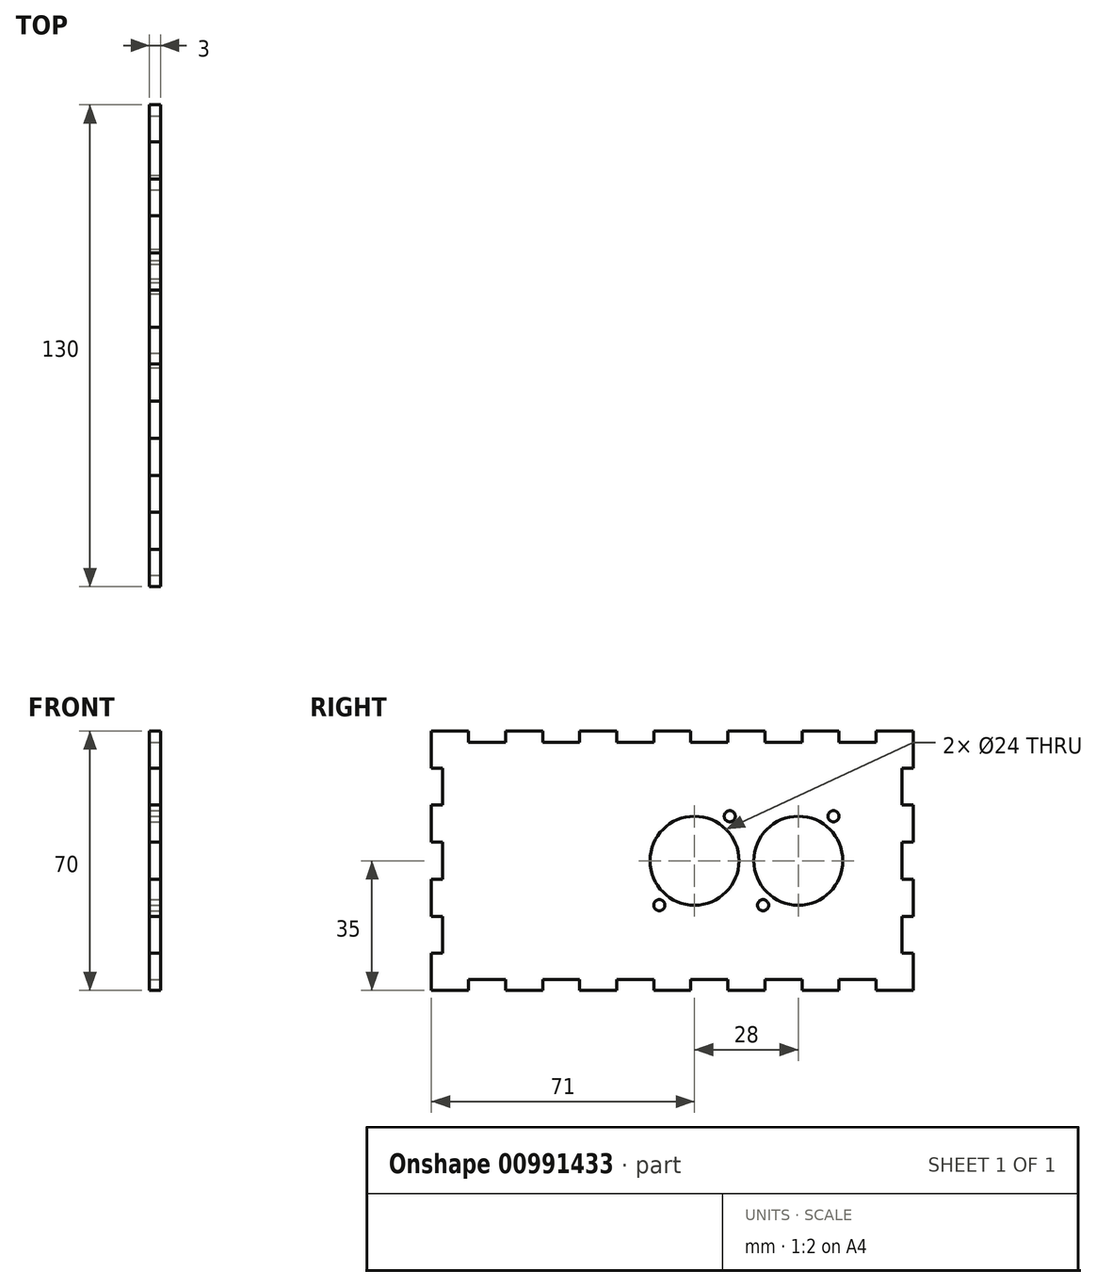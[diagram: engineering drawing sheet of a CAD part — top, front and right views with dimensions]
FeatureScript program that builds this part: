
annotation { "Feature Type Name" : "Feature", "Feature Type Description" : "" }
export const myFeature = defineFeature(function(context is Context, id is Id, definition is map)
    precondition{}
    {
        {
            var Q0;
            Q0=qCreatedBy(makeId("Right.planeOp"),FACE);
            var sketch = newSketch(context, id + "F0", { "sketchPlane" : qUnion([Q0])});
            skLineSegment(sketch, "E0.bottom", {"start": v(65, -35) * mm, "end": v(-65, -35) * mm});
            skLineSegment(sketch, "E0.top", {"start": v(65, 35) * mm, "end": v(-65, 35) * mm});
            skLineSegment(sketch, "E0.left", {"start": v(65, -35) * mm, "end": v(65, 35) * mm});
            skLineSegment(sketch, "E0.right", {"start": v(-65, -35) * mm, "end": v(-65, 35) * mm});
            skPoint(sketch, "E0.middle", {"position": v(0, 0) * mm});
            skSolve(sketch);
        }
        {
            var Q0;
            Q0 = qSketchRegion(id + "F0", true);
            extrude(context, id + "F1", {"entities" : qUnion([Q0]), "depth" : 3 * mm, "offsetDistance" : 25 * mm});
        }
        {
            var Q0;
            Q0=makeQuery(id+"F1.opExtrude","CAP_FACE",FACE,{"disambiguationData":[OSD([sQuery(id+"F0.wireOp",EDGE,"E0.bottom"),sQuery(id+"F0.wireOp",EDGE,"E0.top"),sQuery(id+"F0.wireOp",EDGE,"E0.left"),sQuery(id+"F0.wireOp",EDGE,"E0.right")])],"isStart":false});
            var sketch = newSketch(context, id + "F2", { "sketchPlane" : qUnion([Q0])});
            skLineSegment(sketch, "E1.bottom", {"start": v(-65, 25) * mm, "end": v(-62, 25) * mm});
            skLineSegment(sketch, "E1.top", {"start": v(-65, 15) * mm, "end": v(-62, 15) * mm});
            skLineSegment(sketch, "E1.left", {"start": v(-65, 25) * mm, "end": v(-65, 15) * mm});
            skLineSegment(sketch, "E1.right", {"start": v(-62, 25) * mm, "end": v(-62, 15) * mm});
            skLineSegment(sketch, "E2.0.1.0", {"start": v(-65, 5) * mm, "end": v(-65, -5) * mm});
            skLineSegment(sketch, "E2.0.1.1", {"start": v(-65, 5) * mm, "end": v(-62, 5) * mm});
            skLineSegment(sketch, "E2.0.1.2", {"start": v(-62, 5) * mm, "end": v(-62, -5) * mm});
            skLineSegment(sketch, "E2.0.1.3", {"start": v(-65, -5) * mm, "end": v(-62, -5) * mm});
            skLineSegment(sketch, "E2.0.2.0", {"start": v(-65, -15) * mm, "end": v(-65, -25) * mm});
            skLineSegment(sketch, "E2.0.2.1", {"start": v(-65, -15) * mm, "end": v(-62, -15) * mm});
            skLineSegment(sketch, "E2.0.2.2", {"start": v(-62, -15) * mm, "end": v(-62, -25) * mm});
            skLineSegment(sketch, "E2.0.2.3", {"start": v(-65, -25) * mm, "end": v(-62, -25) * mm});
            skLineSegment(sketch, "E2.direction1", {"start": v(-65, 15) * mm, "end": v(-35, 15) * mm, "construction": true});
            skLineSegment(sketch, "E2.direction2", {"start": v(-65, 15) * mm, "end": v(-65, -5) * mm, "construction": true});
            skLineSegment(sketch, "E3", {"start": v(0, 35) * mm, "end": v(0, -35) * mm, "construction": true});
            skLineSegment(sketch, "E4.MirrorCS", {"start": v(65, 5) * mm, "end": v(65, -5) * mm});
            skLineSegment(sketch, "E5.MirrorCS", {"start": v(62, 5) * mm, "end": v(62, -5) * mm});
            skLineSegment(sketch, "E6.MirrorCS", {"start": v(65, -5) * mm, "end": v(62, -5) * mm});
            skLineSegment(sketch, "E7.MirrorCS", {"start": v(65, 15) * mm, "end": v(65, -5) * mm, "construction": true});
            skLineSegment(sketch, "E8.MirrorCS", {"start": v(65, 25) * mm, "end": v(62, 25) * mm});
            skLineSegment(sketch, "E9.MirrorCS", {"start": v(65, -15) * mm, "end": v(65, -25) * mm});
            skLineSegment(sketch, "E10.MirrorCS", {"start": v(65, 15) * mm, "end": v(62, 15) * mm});
            skLineSegment(sketch, "E11.MirrorCS", {"start": v(62, -15) * mm, "end": v(62, -25) * mm});
            skLineSegment(sketch, "E12.MirrorCS", {"start": v(62, 25) * mm, "end": v(62, 15) * mm});
            skLineSegment(sketch, "E13.MirrorCS", {"start": v(65, -25) * mm, "end": v(62, -25) * mm});
            skLineSegment(sketch, "E14.MirrorCS", {"start": v(65, -15) * mm, "end": v(62, -15) * mm});
            skLineSegment(sketch, "E15.MirrorCS", {"start": v(65, 25) * mm, "end": v(65, 15) * mm});
            skLineSegment(sketch, "E16.MirrorCS", {"start": v(65, 5) * mm, "end": v(62, 5) * mm});
            skLineSegment(sketch, "E17", {"start": v(-65, 0) * mm, "end": v(65, 0) * mm, "construction": true});
            skLineSegment(sketch, "E18.bottom", {"start": v(-55, -35) * mm, "end": v(-45, -35) * mm});
            skLineSegment(sketch, "E18.top", {"start": v(-55, -32) * mm, "end": v(-45, -32) * mm});
            skLineSegment(sketch, "E18.left", {"start": v(-55, -35) * mm, "end": v(-55, -32) * mm});
            skLineSegment(sketch, "E18.right", {"start": v(-45, -35) * mm, "end": v(-45, -32) * mm});
            skLineSegment(sketch, "E19.1.0.0", {"start": v(-35, -35) * mm, "end": v(-35, -32) * mm});
            skLineSegment(sketch, "E19.1.0.1", {"start": v(-35, -32) * mm, "end": v(-25, -32) * mm});
            skLineSegment(sketch, "E19.1.0.2", {"start": v(-25, -35) * mm, "end": v(-25, -32) * mm});
            skLineSegment(sketch, "E19.1.0.3", {"start": v(-35, -35) * mm, "end": v(-25, -35) * mm});
            skLineSegment(sketch, "E19.2.0.0", {"start": v(-15, -35) * mm, "end": v(-15, -32) * mm});
            skLineSegment(sketch, "E19.2.0.1", {"start": v(-15, -32) * mm, "end": v(-5, -32) * mm});
            skLineSegment(sketch, "E19.2.0.2", {"start": v(-5, -35) * mm, "end": v(-5, -32) * mm});
            skLineSegment(sketch, "E19.2.0.3", {"start": v(-15, -35) * mm, "end": v(-5, -35) * mm});
            skLineSegment(sketch, "E19.3.0.0", {"start": v(5, -35) * mm, "end": v(5, -32) * mm});
            skLineSegment(sketch, "E19.3.0.1", {"start": v(5, -32) * mm, "end": v(15, -32) * mm});
            skLineSegment(sketch, "E19.3.0.2", {"start": v(15, -35) * mm, "end": v(15, -32) * mm});
            skLineSegment(sketch, "E19.3.0.3", {"start": v(5, -35) * mm, "end": v(15, -35) * mm});
            skLineSegment(sketch, "E19.4.0.0", {"start": v(25, -35) * mm, "end": v(25, -32) * mm});
            skLineSegment(sketch, "E19.4.0.1", {"start": v(25, -32) * mm, "end": v(35, -32) * mm});
            skLineSegment(sketch, "E19.4.0.2", {"start": v(35, -35) * mm, "end": v(35, -32) * mm});
            skLineSegment(sketch, "E19.4.0.3", {"start": v(25, -35) * mm, "end": v(35, -35) * mm});
            skLineSegment(sketch, "E19.5.0.0", {"start": v(45, -35) * mm, "end": v(45, -32) * mm});
            skLineSegment(sketch, "E19.5.0.1", {"start": v(45, -32) * mm, "end": v(55, -32) * mm});
            skLineSegment(sketch, "E19.5.0.2", {"start": v(55, -35) * mm, "end": v(55, -32) * mm});
            skLineSegment(sketch, "E19.5.0.3", {"start": v(45, -35) * mm, "end": v(55, -35) * mm});
            skLineSegment(sketch, "E19.direction1", {"start": v(-55, -35) * mm, "end": v(-35, -35) * mm, "construction": true});
            skLineSegment(sketch, "E20.MirrorCS", {"start": v(-55, 35) * mm, "end": v(-45, 35) * mm});
            skLineSegment(sketch, "E21.MirrorCS", {"start": v(-25, 35) * mm, "end": v(-25, 32) * mm});
            skLineSegment(sketch, "E22.MirrorCS", {"start": v(45, 32) * mm, "end": v(55, 32) * mm});
            skLineSegment(sketch, "E23.MirrorCS", {"start": v(45, 35) * mm, "end": v(55, 35) * mm});
            skLineSegment(sketch, "E24.MirrorCS", {"start": v(-35, 35) * mm, "end": v(-25, 35) * mm});
            skLineSegment(sketch, "E25.MirrorCS", {"start": v(-35, 32) * mm, "end": v(-25, 32) * mm});
            skLineSegment(sketch, "E26.MirrorCS", {"start": v(-5, 35) * mm, "end": v(-5, 32) * mm});
            skLineSegment(sketch, "E27.MirrorCS", {"start": v(-55, 35) * mm, "end": v(-55, 32) * mm});
            skLineSegment(sketch, "E28.MirrorCS", {"start": v(5, 32) * mm, "end": v(15, 32) * mm});
            skLineSegment(sketch, "E29.MirrorCS", {"start": v(55, 35) * mm, "end": v(55, 32) * mm});
            skLineSegment(sketch, "E30.MirrorCS", {"start": v(5, 35) * mm, "end": v(15, 35) * mm});
            skLineSegment(sketch, "E31.MirrorCS", {"start": v(-15, 32) * mm, "end": v(-5, 32) * mm});
            skLineSegment(sketch, "E32.MirrorCS", {"start": v(5, 35) * mm, "end": v(5, 32) * mm});
            skLineSegment(sketch, "E33.MirrorCS", {"start": v(-55, 32) * mm, "end": v(-45, 32) * mm});
            skLineSegment(sketch, "E34.MirrorCS", {"start": v(-55, 35) * mm, "end": v(-35, 35) * mm, "construction": true});
            skLineSegment(sketch, "E35.MirrorCS", {"start": v(35, 35) * mm, "end": v(35, 32) * mm});
            skLineSegment(sketch, "E36.MirrorCS", {"start": v(25, 35) * mm, "end": v(25, 32) * mm});
            skLineSegment(sketch, "E37.MirrorCS", {"start": v(-15, 35) * mm, "end": v(-5, 35) * mm});
            skLineSegment(sketch, "E38.MirrorCS", {"start": v(15, 35) * mm, "end": v(15, 32) * mm});
            skLineSegment(sketch, "E39.MirrorCS", {"start": v(25, 32) * mm, "end": v(35, 32) * mm});
            skLineSegment(sketch, "E40.MirrorCS", {"start": v(-15, 35) * mm, "end": v(-15, 32) * mm});
            skLineSegment(sketch, "E41.MirrorCS", {"start": v(45, 35) * mm, "end": v(45, 32) * mm});
            skLineSegment(sketch, "E42.MirrorCS", {"start": v(-35, 35) * mm, "end": v(-35, 32) * mm});
            skLineSegment(sketch, "E43.MirrorCS", {"start": v(25, 35) * mm, "end": v(35, 35) * mm});
            skLineSegment(sketch, "E44.MirrorCS", {"start": v(-45, 35) * mm, "end": v(-45, 32) * mm});
            skSolve(sketch);
        }
        {
            var Q0;
            Q0 = qSketchRegion(id + "F2", true);
            extrude(context, id + "F3", {"entities" : qUnion([Q0]), "operationType" : NewBodyOperationType.REMOVE, "endBound" : BoundingType.THROUGH_ALL, "oppositeDirection" : true, "depth" : 25 * mm, "offsetDistance" : 25 * mm});
        }
        {
            var Q0;
            Q0=makeQuery(id+"F1.opExtrude","CAP_FACE",FACE,{"disambiguationData":[OSD([sQuery(id+"F0.wireOp",EDGE,"E0.bottom"),sQuery(id+"F0.wireOp",EDGE,"E0.top"),sQuery(id+"F0.wireOp",EDGE,"E0.left"),sQuery(id+"F0.wireOp",EDGE,"E0.right")])],"isStart":false});
            var sketch = newSketch(context, id + "F4", { "sketchPlane" : qUnion([Q0])});
            skLineSegment(sketch, "E45.bottom", {"start": v(47, 15.5) * mm, "end": v(21, 15.5) * mm, "construction": true});
            skLineSegment(sketch, "E45.top", {"start": v(47, -15.5) * mm, "end": v(21, -15.5) * mm, "construction": true});
            skLineSegment(sketch, "E45.left", {"start": v(47, 15.5) * mm, "end": v(47, -15.5) * mm, "construction": true});
            skLineSegment(sketch, "E45.right", {"start": v(21, 15.5) * mm, "end": v(21, -15.5) * mm, "construction": true});
            skLineSegment(sketch, "E46", {"start": v(47, 15.5) * mm, "end": v(21, -15.5) * mm, "construction": true});
            skCircle(sketch, "E47", {"center": v(34, 0) * mm, "radius": 12 * mm});
            skLineSegment(sketch, "E48.bottom", {"start": v(24.5, 12) * mm, "end": v(43.5, 12) * mm, "construction": true});
            skLineSegment(sketch, "E48.top", {"start": v(24.5, -12) * mm, "end": v(43.5, -12) * mm, "construction": true});
            skLineSegment(sketch, "E48.left", {"start": v(24.5, 12) * mm, "end": v(24.5, -12) * mm, "construction": true});
            skLineSegment(sketch, "E48.right", {"start": v(43.5, 12) * mm, "end": v(43.5, -12) * mm, "construction": true});
            skCircle(sketch, "E49", {"center": v(43.5, 12) * mm, "radius": 1.5 * mm});
            skCircle(sketch, "E50", {"center": v(24.5, -12) * mm, "radius": 1.5 * mm});
            skLineSegment(sketch, "E51", {"start": v(62, 0) * mm, "end": v(-62, 0) * mm, "construction": true});
            skCircle(sketch, "E52.1.0.0", {"center": v(6, 0) * mm, "radius": 12 * mm});
            skCircle(sketch, "E52.1.0.1", {"center": v(-3.5, -12) * mm, "radius": 1.5 * mm});
            skCircle(sketch, "E52.1.0.2", {"center": v(15.5, 12) * mm, "radius": 1.5 * mm});
            skLineSegment(sketch, "E52.1.0.3", {"start": v(-7, 15.5) * mm, "end": v(-7, -15.5) * mm, "construction": true});
            skLineSegment(sketch, "E52.1.0.4", {"start": v(19, 15.5) * mm, "end": v(19, -15.5) * mm, "construction": true});
            skLineSegment(sketch, "E52.1.0.5", {"start": v(19, 15.5) * mm, "end": v(-7, 15.5) * mm, "construction": true});
            skLineSegment(sketch, "E52.1.0.6", {"start": v(19, -15.5) * mm, "end": v(-7, -15.5) * mm, "construction": true});
            skLineSegment(sketch, "E52.direction1", {"start": v(24.5, -12) * mm, "end": v(-3.5, -12) * mm, "construction": true});
            skSolve(sketch);
        }
        {
            var Q0;
            Q0 = qSketchRegion(id + "F4", true);
            extrude(context, id + "F5", {"entities" : qUnion([Q0]), "operationType" : NewBodyOperationType.REMOVE, "endBound" : BoundingType.THROUGH_ALL, "oppositeDirection" : true, "depth" : 25 * mm, "offsetDistance" : 25 * mm});
        }
    });
